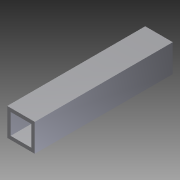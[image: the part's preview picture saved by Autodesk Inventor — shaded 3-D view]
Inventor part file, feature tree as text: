
AUTODESK INVENTOR PART (.ipt)
format: ipt  version: 2012 (Build 160160000, 160)  size: 76,800 bytes
history: native  units: in
note: dims shown in document units (in); Inventor stores cm internally (conversion verified against a paired STEP export)
features: extrude x1, sketch x1
ambient origin geometry x8: Origin, YZ Plane, XZ Plane, XY Plane, X Axis, Y Axis, Z Axis, Center Point
bodies: Solid1 (feature_tree)
feature tree (2):
  extrude  "Extrusion1"  Depth=0.125in
  sketch  "Sketch1"  dims[d0=0.125in d1=0.125in d2=0.125in d3=0.125in d4=1.0in d5=1.0in d6=5.0in d7=0.0in]
